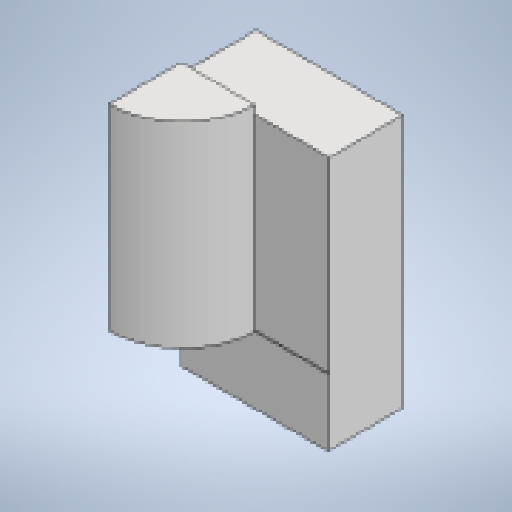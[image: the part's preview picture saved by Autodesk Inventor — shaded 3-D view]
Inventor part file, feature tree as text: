
AUTODESK INVENTOR PART (.ipt)
format: ipt  version: 2025.1 (Build 291241020, 241B)  size: 145,920 bytes
history: native  units: mm
features: extrude x3, sketch x3, projected_geometry x2
ambient origin geometry x8: Origin, YZ Plane, XZ Plane, XY Plane, X Axis, Y Axis, Z Axis, Center Point
bodies: Solid1 (feature_tree)
feature tree (8):
  extrude  "Extrusion1"  Depth=550.0mm
  extrude  "Extrusion2"  Depth=500.0mm
  extrude  "Extrusion3"  Depth=1169.0mm TaperAngle=0.0deg
  sketch  "Sketch1"  dims[d0=1100.0mm d1=550.0mm]
  sketch  "Sketch2"  dims[d2=1900.0mm d3=0.0mm d4=500.0mm]
  projected_geometry  "Projected Loop1"
  sketch  "Sketch3"  dims[d5=10.0mm d6=0.0mm d7=1169.0mm d8=0.0mm]
  projected_geometry  "Projected Loop2"
